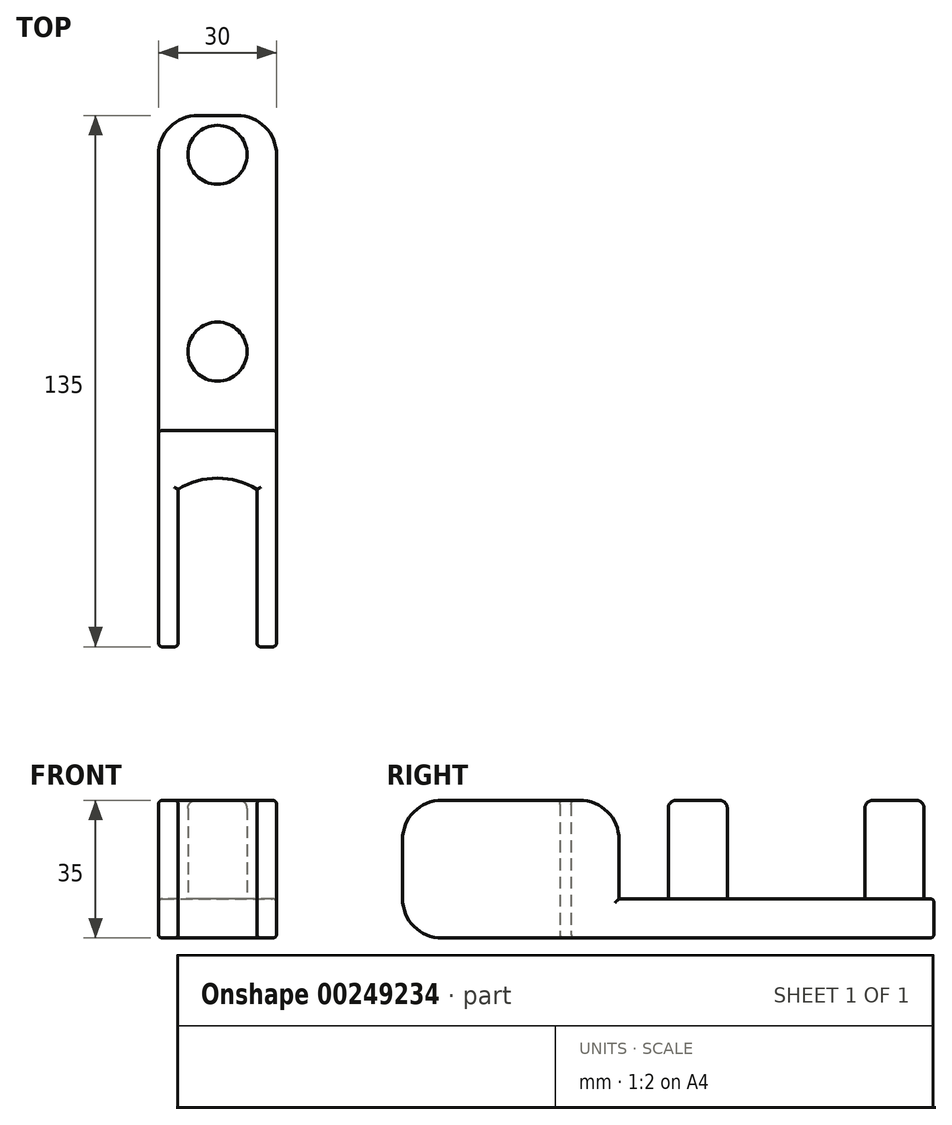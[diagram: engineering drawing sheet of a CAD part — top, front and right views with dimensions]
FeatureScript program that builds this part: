
annotation { "Feature Type Name" : "Feature", "Feature Type Description" : "" }
export const myFeature = defineFeature(function(context is Context, id is Id, definition is map)
    precondition{}
    {
        {
            var Q0;
            Q0=qCreatedBy(makeId("Top.planeOp"),FACE);
            var sketch = newSketch(context, id + "F0", { "sketchPlane" : qUnion([Q0])});
            skLineSegment(sketch, "E0", {"start": v(0, 135) * mm, "end": v(0, 0) * mm});
            skLineSegment(sketch, "E1", {"start": v(0, 0) * mm, "end": v(5, 0) * mm});
            skLineSegment(sketch, "E2", {"start": v(5, 0) * mm, "end": v(5, 40) * mm});
            skLineSegment(sketch, "E3", {"start": v(5, 40) * mm, "end": v(25, 40) * mm});
            skLineSegment(sketch, "E4", {"start": v(25, 40) * mm, "end": v(25, 0) * mm});
            skLineSegment(sketch, "E5", {"start": v(25, 0) * mm, "end": v(30, 0) * mm});
            skLineSegment(sketch, "E6", {"start": v(30, 0) * mm, "end": v(30, 135) * mm});
            skLineSegment(sketch, "E7", {"start": v(30, 135) * mm, "end": v(0, 135) * mm});
            skLineSegment(sketch, "E8", {"start": v(0, 55) * mm, "end": v(30, 55) * mm});
            skArc(sketch, "E9", {"start": v(25, 40) * mm, "mid": v(15, 42.85) * mm, "end": v(5, 40) * mm});
            skSolve(sketch);
        }
        {
            var Q0;
            {var subQ1=sQuery(id+"F0.wireOp",EDGE,"E1");Q0=makeQuery(id+"F0.imprint","IMPRINT",FACE,{"disambiguationData":[TD([[makeQuery(id+"F0.imprint","IMPRINT",EDGE,{"derivedFrom":subQ1}),1.0]])]});}
            extrude(context, id + "F1", {"entities" : qUnion([Q0]), "depth" : 35 * mm});
        }
        {
            var Q0;
            {var subQ0=sQuery(id+"F0.wireOp",EDGE,"E7");Q0=makeQuery(id+"F0.imprint","IMPRINT",FACE,{"disambiguationData":[TD([[makeQuery(id+"F0.imprint","IMPRINT",EDGE,{"derivedFrom":subQ0}),1.0]])]});}
            extrude(context, id + "F2", {"entities" : qUnion([Q0]), "operationType" : NewBodyOperationType.ADD, "depth" : 10 * mm});
        }
        {
            var Q0;
            Q0=makeQuery(id+"F2.opExtrude","CAP_FACE",FACE,{"disambiguationData":[OSD([sQuery(id+"F0.wireOp",EDGE,"E0"),sQuery(id+"F0.wireOp",EDGE,"E6"),sQuery(id+"F0.wireOp",EDGE,"E7"),sQuery(id+"F0.wireOp",EDGE,"E8")])],"isStart":false});
            var sketch = newSketch(context, id + "F3", { "sketchPlane" : qUnion([Q0])});
            skCircle(sketch, "E10", {"center": v(15, 125) * mm, "radius": 7.5 * mm});
            skPoint(sketch, "E10.centerSnap0", {"position": v(15, 135) * mm});
            skCircle(sketch, "E11", {"center": v(15, 75) * mm, "radius": 7.5 * mm});
            skSolve(sketch);
        }
        {
            var Q0;
            Q0=makeQuery(id+"F3.imprint","IMPRINT",FACE,{"disambiguationData":[TD([[makeQuery(id+"F3.imprint","IMPRINT",EDGE,{"derivedFrom":sQuery(id+"F3.wireOp",EDGE,"E10")}),1.0]])]});
            var Q1;
            Q1=makeQuery(id+"F3.imprint","IMPRINT",FACE,{"disambiguationData":[TD([[makeQuery(id+"F3.imprint","IMPRINT",EDGE,{"derivedFrom":sQuery(id+"F3.wireOp",EDGE,"E11")}),1.0]])]});
            var Q2;
            Q2=makeQuery(id+"F1.opExtrude","CAP_FACE",FACE,{"disambiguationData":[OSD([sQuery(id+"F0.wireOp",EDGE,"E0"),sQuery(id+"F0.wireOp",EDGE,"E1"),sQuery(id+"F0.wireOp",EDGE,"E2"),sQuery(id+"F0.wireOp",EDGE,"E3"),sQuery(id+"F0.wireOp",EDGE,"E4"),sQuery(id+"F0.wireOp",EDGE,"E5"),sQuery(id+"F0.wireOp",EDGE,"E6"),sQuery(id+"F0.wireOp",EDGE,"E8")])],"isStart":false});
            extrude(context, id + "F4", {"entities" : qUnion([Q0, Q1]), "operationType" : NewBodyOperationType.ADD, "endBound" : BoundingType.UP_TO_SURFACE, "endBoundEntityFace" : qUnion([Q2]), "depth" : 25 * mm});
        }
        {
            var Q0;
            Q0=makeQuery(id+"F2.opExtrude","SWEPT_EDGE",EDGE,{"disambiguationData":[OSD([sQuery(id+"F0.wireOp",EDGE,"E0"),sQuery(id+"F0.wireOp",EDGE,"E7")])]});
            var Q1;
            Q1=makeQuery(id+"F2.opExtrude","SWEPT_EDGE",EDGE,{"disambiguationData":[OSD([sQuery(id+"F0.wireOp",EDGE,"E6"),sQuery(id+"F0.wireOp",EDGE,"E7")])]});
            var Q2;
            Q2=makeQuery(id+"F1.opExtrude","CAP_EDGE",EDGE,{"disambiguationData":[OSD([sQuery(id+"F0.wireOp",EDGE,"E8")])],"isStart":false});
            var Q3;
            Q3=makeQuery(id+"F1.opExtrude","CAP_EDGE",EDGE,{"disambiguationData":[OSD([sQuery(id+"F0.wireOp",EDGE,"E5")])],"isStart":false});
            var Q4;
            Q4=makeQuery(id+"F1.opExtrude","CAP_EDGE",EDGE,{"disambiguationData":[OSD([sQuery(id+"F0.wireOp",EDGE,"E1")])],"isStart":false});
            var Q5;
            Q5=makeQuery(id+"F1.opExtrude","CAP_EDGE",EDGE,{"disambiguationData":[OSD([sQuery(id+"F0.wireOp",EDGE,"E5")])],"isStart":true});
            var Q6;
            Q6=makeQuery(id+"F1.opExtrude","CAP_EDGE",EDGE,{"disambiguationData":[OSD([sQuery(id+"F0.wireOp",EDGE,"E1")])],"isStart":true});
            fillet(context, id + "F5", {"entities" : qUnion([Q0, Q1, Q2, Q3, Q4, Q5, Q6]), "radius" : 10 * mm, "tangentPropagation" : true, "allowEdgeOverflow" : false});
        }
        {
            var Q0;
            {var subQ0=sQuery(id+"F0.wireOp",EDGE,"E6");Q0=makeQuery(id+"F2.boolean.opBoolean","MERGE",FACE,{"derivedFrom":[makeQuery(id+"F1.opExtrude","SWEPT_FACE",FACE,{"disambiguationData":[OSD([subQ0])]}),makeQuery(id+"F2.opExtrude","SWEPT_FACE",FACE,{"disambiguationData":[OSD([subQ0])]})]});}
            fillet(context, id + "F6", {"entities" : qUnion([Q0]), "radius" : 1 * mm, "tangentPropagation" : true, "allowEdgeOverflow" : false});
        }
        {
            var Q0;
            Q0=makeQuery(id+"F4.opExtrude","CAP_EDGE",EDGE,{"disambiguationData":[OSD([sQuery(id+"F3.wireOp",EDGE,"E11")])],"isStart":true});
            var Q1;
            Q1=makeQuery(id+"F4.opExtrude","CAP_EDGE",EDGE,{"disambiguationData":[OSD([sQuery(id+"F3.wireOp",EDGE,"E10")])],"isStart":true});
            var Q2;
            Q2=makeQuery(id+"F4.opExtrude","CAP_EDGE",EDGE,{"disambiguationData":[OSD([sQuery(id+"F3.wireOp",EDGE,"E10")])],"isStart":false});
            var Q3;
            Q3=makeQuery(id+"F4.opExtrude","CAP_EDGE",EDGE,{"disambiguationData":[OSD([sQuery(id+"F3.wireOp",EDGE,"E11")])],"isStart":false});
            fillet(context, id + "F7", {"entities" : qUnion([Q0, Q1, Q2, Q3]), "radius" : 2 * mm, "tangentPropagation" : true, "allowEdgeOverflow" : false});
        }
        {
            var Q0;
            Q0=makeQuery(id+"F1.opExtrude","CAP_EDGE",EDGE,{"disambiguationData":[OSD([sQuery(id+"F0.wireOp",EDGE,"E2")])],"isStart":false});
            var Q1;
            Q1=makeQuery(id+"F1.opExtrude","CAP_EDGE",EDGE,{"disambiguationData":[OSD([sQuery(id+"F0.wireOp",EDGE,"E9")])],"isStart":false});
            var Q2;
            Q2=makeQuery(id+"F1.opExtrude","CAP_EDGE",EDGE,{"disambiguationData":[OSD([sQuery(id+"F0.wireOp",EDGE,"E4")])],"isStart":false});
            var Q3;
            Q3=makeQuery(id+"F1.opExtrude","CAP_EDGE",EDGE,{"disambiguationData":[OSD([sQuery(id+"F0.wireOp",EDGE,"E9")])],"isStart":true});
            fillet(context, id + "F8", {"entities" : qUnion([Q0, Q1, Q2, Q3]), "radius" : 1 * mm, "tangentPropagation" : true, "allowEdgeOverflow" : false});
        }
    });
